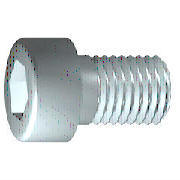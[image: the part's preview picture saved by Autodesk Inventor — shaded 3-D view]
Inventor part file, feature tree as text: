
AUTODESK INVENTOR PART (.ipt)
format: ipt  version: 2020 (Build 240168000, 168)  size: 199,168 bytes
history: native  units: mm (DEFAULTED — no unit token found)
features: sketch x2, other x1, extrude x1, plane x1, fillet x1
ambient origin geometry x7: Origin, YZ Plane, XY Plane, X Axis, Y Axis, Z Axis, Center Point
bodies: Solid1 (feature_tree)
feature tree (6):
  other  "Bryła"
  extrude  "Szczelina"  Depth=3.9mm
  plane  "Work Plane1"
  fillet  "Fillet2"  Radius=0.429515mm
  sketch  "Szkic1"
  sketch  "Szkic2"
